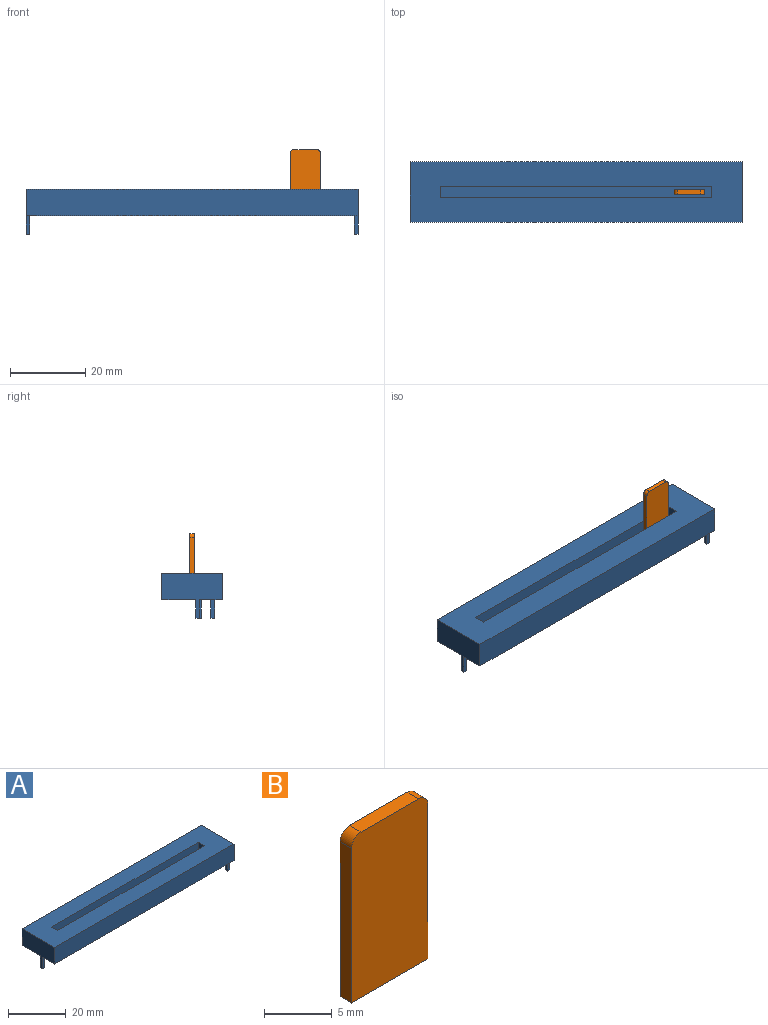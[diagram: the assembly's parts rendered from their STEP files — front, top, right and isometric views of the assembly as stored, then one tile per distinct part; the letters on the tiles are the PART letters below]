
ASSEMBLY  parts=2 mates=1
PART A: 23 faces, bbox 88x16x12 mm
  f0: plane 88x16mm, normal (0,0,1), area 1192mm2, adj f1,f2,f3,f4,f6,f7,f8,f9
  f1: plane 88x7mm, normal (0,1,0), area 616mm2, adj f0,f2,f4,f5
  f2: plane 16x12mm, normal (-1,0,0), area 117mm2, adj f0,f1,f3,f5,f11,f12,f14
  f3: plane 88x7mm, normal (0,-1,0), area 616mm2, adj f0,f2,f4,f5
  f4: plane 16x12mm, normal (1,0,0), area 122mm2, adj f0,f1,f3,f5,f15,f17,f18,f19
  f5: plane 88x16mm, normal (0,0,-1), area 1405mm2, adj f1,f2,f3,f4,f11,f12,f13,f15
  f6: plane 72x5mm, normal (0,-1,0), area 360mm2, adj f0,f7,f9,f10
  f7: plane 5x3mm, normal (1,0,0), area 15mm2, adj f0,f6,f8,f10
  f8: plane 72x5mm, normal (0,1,0), area 360mm2, adj f0,f7,f9,f10
  f9: plane 5x3mm, normal (-1,0,0), area 15mm2, adj f0,f6,f8,f10
  f10: plane 72x3mm, normal (0,0,1), area 216mm2, adj f6,f7,f8,f9
  f11: plane 5x1mm, normal (0,-1,0), area 5mm2, adj f2,f5,f13,f14
  f12: plane 5x1mm, normal (0,1,0), area 5mm2, adj f2,f5,f13,f14
  f13: plane 5x1mm, normal (1,0,0), area 5mm2, adj f5,f11,f12,f14
  f14: plane 1x1mm, normal (0,0,-1), area 1mm2, adj f2,f11,f12,f13
  f15: plane 5x1mm, normal (0,-1,0), area 5mm2, adj f4,f5,f16,f18
  f16: plane 5x1mm, normal (-1,0,0), area 5mm2, adj f5,f15,f17,f18
  f17: plane 5x1mm, normal (0,1,0), area 5mm2, adj f4,f5,f16,f18
  f18: plane 1x1mm, normal (0,0,-1), area 1mm2, adj f4,f15,f16,f17
  f19: plane 5x1mm, normal (0,-1,0), area 5mm2, adj f4,f5,f20,f22
  f20: plane 5x1mm, normal (-1,0,0), area 5mm2, adj f5,f19,f21,f22
  f21: plane 5x1mm, normal (0,1,0), area 5mm2, adj f4,f5,f20,f22
  f22: plane 1x1mm, normal (0,0,-1), area 1mm2, adj f4,f19,f20,f21
PART B: 8 faces, bbox 8x1.2x15 mm
  f0: plane 14x1.2mm, normal (-1,0,0), area 16.8mm2, adj f1,f4,f5,f7
  f1: plane 8x1.2mm, normal (0,0,-1), area 9.6mm2, adj f0,f2,f4,f5
  f2: plane 14x1.2mm, normal (1,0,0), area 16.8mm2, adj f1,f4,f5,f6
  f3: plane 6x1.2mm, normal (0,0,1), area 7.2mm2, adj f4,f5,f6,f7
  f4: plane 15x8mm, normal (0,-1,0), area 119.6mm2, adj f0,f1,f2,f3,f6,f7
  f5: plane 15x8mm, normal (0,1,0), area 119.6mm2, adj f0,f1,f2,f3,f6,f7
  f6: cylinder r=1mm len=1.2mm, axis (0,-1,0), area 1.9mm2, adj f2,f3,f4,f5
  f7: cylinder r=1mm len=1.2mm, axis (0,1,0), area 1.9mm2, adj f0,f3,f4,f5
PLACE A t=(-63.57,-20.13,19.8)mm
PLACE B t=(-37.57,-19.53,22.3)mm
MATE slider A.f9 <-> B.f2  axis (1,0,0) through (-27.57,-20.13,24.3)mm
